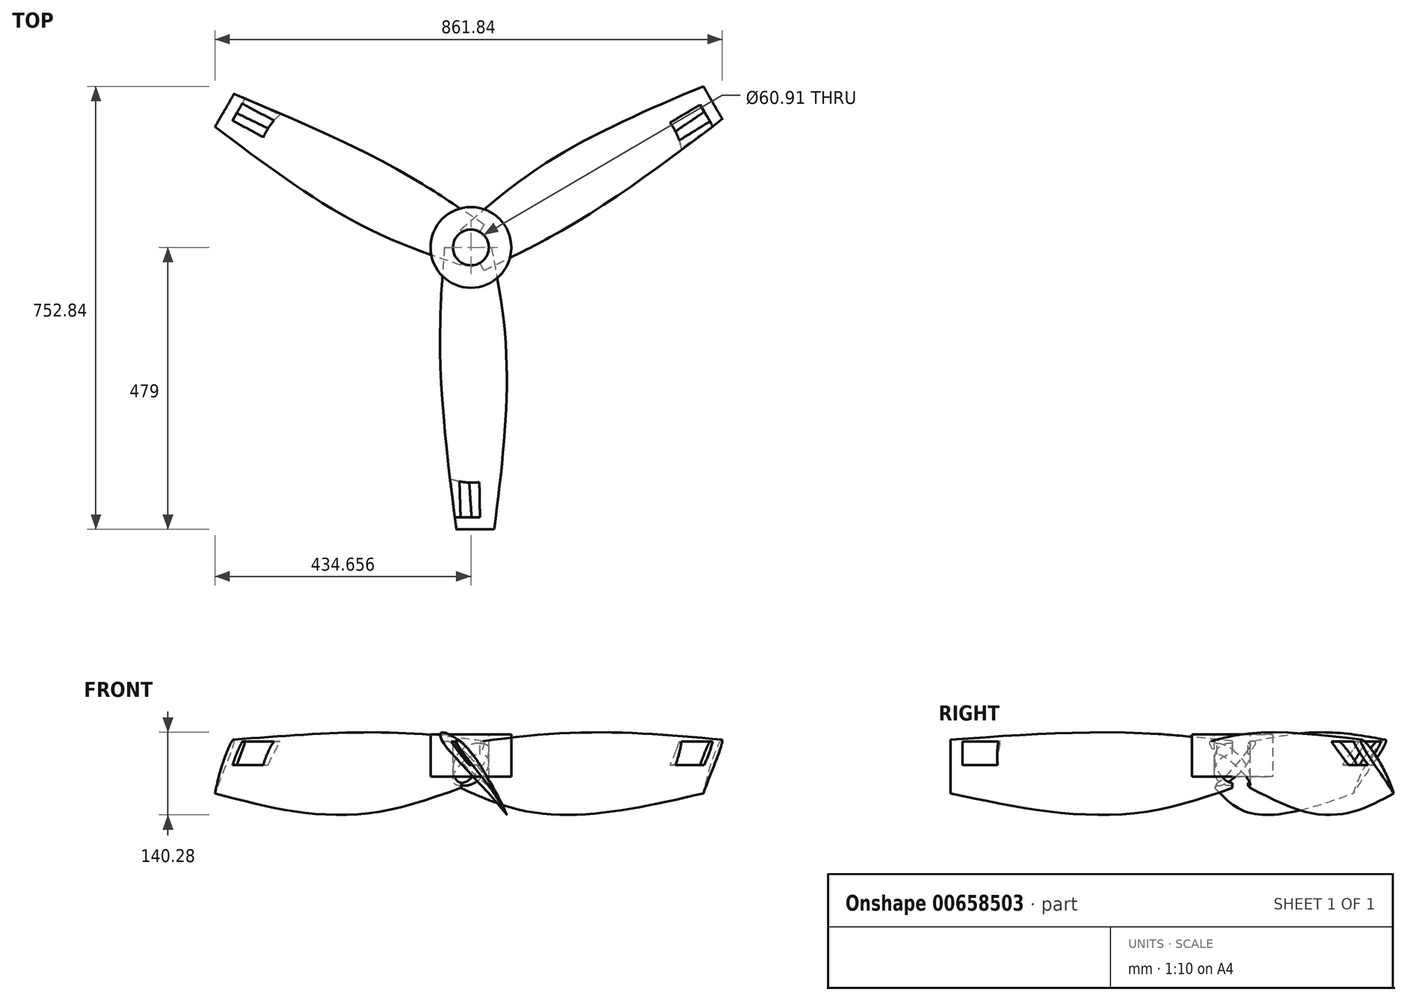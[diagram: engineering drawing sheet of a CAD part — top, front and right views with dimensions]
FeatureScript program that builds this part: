
annotation { "Feature Type Name" : "Feature", "Feature Type Description" : "" }
export const myFeature = defineFeature(function(context is Context, id is Id, definition is map)
    precondition{}
    {
        {
            var Q0;
            Q0=qCreatedBy(makeId("Front.planeOp"),FACE);
            var sketch = newSketch(context, id + "F0", { "sketchPlane" : qUnion([Q0])});
            skLineSegment(sketch, "E0", {"start": v(-19.7, 19.7) * mm, "end": v(0, 0) * mm, "construction": true});
            skLineSegment(sketch, "E1", {"start": v(0, 0) * mm, "end": v(19.7, -19.7) * mm, "construction": true});
            skLineSegment(sketch, "E2", {"start": v(19.7, -19.7) * mm, "end": v(39.39, -39.39) * mm, "construction": true});
            skLineSegment(sketch, "E3", {"start": v(39.39, -39.39) * mm, "end": v(59.08, -59.08) * mm, "construction": true});
            skLineSegment(sketch, "E4", {"start": v(0, 0) * mm, "end": v(7.36, 7.36) * mm, "construction": true});
            skLineSegment(sketch, "E5", {"start": v(-19.7, 19.7) * mm, "end": v(-16.01, 23.38) * mm, "construction": true});
            skFitSpline(sketch, "E6", {"points": [v(-19.7, 19.7) * mm, v(7.36, 7.36) * mm, v(59.08, -59.08) * mm], "startDerivative": vector(29.64, 29.64) * mm, "endDerivative": vector(58.96, -129.41) * mm});
            skPoint(sketch, "E7", {"position": v(3.68, 3.68) * mm});
            skLineSegment(sketch, "E8", {"start": v(-16.01, 23.38) * mm, "end": v(3.68, 3.68) * mm, "construction": true});
            skLineSegment(sketch, "E9", {"start": v(0, 0) * mm, "end": v(-3.68, -3.68) * mm, "construction": true});
            skLineSegment(sketch, "E10", {"start": v(-19.7, 19.7) * mm, "end": v(-23.38, 16.01) * mm, "construction": true});
            skFitSpline(sketch, "E11", {"points": [v(-19.7, 19.7) * mm, v(-3.68, -3.68) * mm, v(59.08, -59.08) * mm], "startDerivative": vector(-30.04, -30.04) * mm, "endDerivative": vector(93.45, -93.45) * mm});
            skLineSegment(sketch, "E12", {"start": v(39.39, -39.39) * mm, "end": v(46.75, -32.02) * mm, "construction": true});
            skLineSegment(sketch, "E13", {"start": v(0, 0) * mm, "end": v(-98.72, 0) * mm, "construction": true});
            skSolve(sketch);
        }
        {
            var Q0;
            Q0=qCreatedBy(makeId("Front.planeOp"),FACE);
            cPlane(context, id + "F1", {"entities" : qUnion([Q0]), "cplaneType" : CPlaneType.OFFSET, "offset" : 125 * mm, "width" : 150 * mm, "height" : 150 * mm});
        }
        {
            var Q0;
            Q0=qCreatedBy(id+"F1.planeOp",FACE);
            var sketch = newSketch(context, id + "F2", { "sketchPlane" : qUnion([Q0])});
            skLineSegment(sketch, "E14", {"start": v(-26.75, 31.88) * mm, "end": v(0, 0) * mm, "construction": true});
            skLineSegment(sketch, "E15", {"start": v(0, 0) * mm, "end": v(26.75, -31.88) * mm, "construction": true});
            skLineSegment(sketch, "E16", {"start": v(26.75, -31.88) * mm, "end": v(53.5, -63.76) * mm, "construction": true});
            skLineSegment(sketch, "E17", {"start": v(53.5, -63.76) * mm, "end": v(80.26, -95.64) * mm, "construction": true});
            skLineSegment(sketch, "E18", {"start": v(0, 0) * mm, "end": v(9.4, 7.88) * mm, "construction": true});
            skLineSegment(sketch, "E19", {"start": v(-26.75, 31.88) * mm, "end": v(-22.06, 35.82) * mm, "construction": true});
            skFitSpline(sketch, "E20", {"points": [v(-26.75, 31.88) * mm, v(9.4, 7.88) * mm, v(80.26, -95.64) * mm], "startDerivative": vector(38.04, 31.92) * mm, "endDerivative": vector(82.71, -189.43) * mm});
            skPoint(sketch, "E21", {"position": v(4.7, 3.94) * mm});
            skLineSegment(sketch, "E22", {"start": v(-22.06, 35.82) * mm, "end": v(4.7, 3.94) * mm, "construction": true});
            skLineSegment(sketch, "E23", {"start": v(0, 0) * mm, "end": v(-4.7, -3.94) * mm, "construction": true});
            skLineSegment(sketch, "E24", {"start": v(-26.75, 31.88) * mm, "end": v(-31.45, 27.94) * mm, "construction": true});
            skFitSpline(sketch, "E25", {"points": [v(-26.75, 31.88) * mm, v(-4.7, -3.94) * mm, v(80.26, -95.64) * mm], "startDerivative": vector(-38.37, -32.2) * mm, "endDerivative": vector(126.81, -151.13) * mm});
            skLineSegment(sketch, "E26", {"start": v(53.5, -63.76) * mm, "end": v(62.9, -55.88) * mm, "construction": true});
            skLineSegment(sketch, "E27", {"start": v(0, 0) * mm, "end": v(-123.06, 0) * mm, "construction": true});
            skSolve(sketch);
        }
        {
            var Q0;
            Q0=qCreatedBy(makeId("Front.planeOp"),FACE);
            cPlane(context, id + "F3", {"entities" : qUnion([Q0]), "cplaneType" : CPlaneType.OFFSET, "offset" : 479 * mm, "width" : 150 * mm, "height" : 150 * mm});
        }
        {
            var Q0;
            Q0=qCreatedBy(id+"F3.planeOp",FACE);
            var sketch = newSketch(context, id + "F4", { "sketchPlane" : qUnion([Q0])});
            skLineSegment(sketch, "E28", {"start": v(0.35, 22.72) * mm, "end": v(16.27, 0) * mm, "construction": true});
            skLineSegment(sketch, "E29", {"start": v(16.27, 0) * mm, "end": v(32.18, -22.72) * mm, "construction": true});
            skLineSegment(sketch, "E30", {"start": v(32.18, -22.72) * mm, "end": v(48.09, -45.45) * mm, "construction": true});
            skLineSegment(sketch, "E31", {"start": v(48.09, -45.45) * mm, "end": v(64, -68.17) * mm, "construction": true});
            skLineSegment(sketch, "E32", {"start": v(16.27, 0) * mm, "end": v(22.38, 4.28) * mm, "construction": true});
            skLineSegment(sketch, "E33", {"start": v(0.35, 22.72) * mm, "end": v(3.41, 24.87) * mm, "construction": true});
            skFitSpline(sketch, "E34", {"points": [v(0.35, 22.72) * mm, v(22.38, 4.28) * mm, v(64, -68.17) * mm], "startDerivative": vector(24.82, 17.38) * mm, "endDerivative": vector(46.62, -128.53) * mm});
            skPoint(sketch, "E35", {"position": v(19.32, 2.14) * mm});
            skLineSegment(sketch, "E36", {"start": v(3.41, 24.87) * mm, "end": v(19.32, 2.14) * mm, "construction": true});
            skLineSegment(sketch, "E37", {"start": v(16.27, 0) * mm, "end": v(13.2, -2.14) * mm, "construction": true});
            skLineSegment(sketch, "E38", {"start": v(0.35, 22.72) * mm, "end": v(-2.7, 20.58) * mm, "construction": true});
            skFitSpline(sketch, "E39", {"points": [v(0.35, 22.72) * mm, v(13.2, -2.14) * mm, v(64, -68.17) * mm], "startDerivative": vector(-25, -17.5) * mm, "endDerivative": vector(75.4, -107.69) * mm});
            skLineSegment(sketch, "E40", {"start": v(48.09, -45.45) * mm, "end": v(54.2, -41.17) * mm, "construction": true});
            skLineSegment(sketch, "E41", {"start": v(19.32, 2.14) * mm, "end": v(-38.53, 2.14) * mm, "construction": true});
            skSolve(sketch);
        }
        {
            var Q0;
            Q0=qSketchRegion(id+"F0",true);
            var Q1;
            Q1=qSketchRegion(id+"F2",true);
            var Q2;
            Q2=qSketchRegion(id+"F4",true);
            var Q3;
            Q3=sQuery(id+"F0.wireOp",VERTEX,"E6.1.internal");
            var Q4;
            Q4=sQuery(id+"F2.wireOp",VERTEX,"E20.1.internal");
            var Q5;
            Q5=sQuery(id+"F4.wireOp",VERTEX,"E32.end");
            loft(context, id + "F5", {"sheetProfilesArray" : [{ "sheetProfileEntities" : qUnion([Q0]) }, { "sheetProfileEntities" : qUnion([Q1]) }, { "sheetProfileEntities" : qUnion([Q2]) }], "matchConnections" : true, "connections" : [{ "connectionEntities" : qUnion([Q3, Q4, Q5]), "connectionEdgeQueries" : qUnion([]), "connectionEdgeParameters" : [] }]});
        }
        {
            var Q0;
            Q0=qCreatedBy(makeId("Top.planeOp"),FACE);
            var sketch = newSketch(context, id + "F6", { "sketchPlane" : qUnion([Q0])});
            skFitSpline(sketch, "E42", {"points": [v(-55.98, -360.47) * mm, v(39.38, -398.87) * mm, v(142.8, -333.19) * mm], "startDerivative": vector(111.22, -150.8) * mm, "endDerivative": vector(54.24, 145.78) * mm});
            skLineSegment(sketch, "E43", {"start": v(-55.98, -360.47) * mm, "end": v(-55.98, -458.75) * mm});
            skLineSegment(sketch, "E44", {"start": v(142.8, -333.19) * mm, "end": v(142.8, -458.75) * mm});
            skLineSegment(sketch, "E45", {"start": v(142.8, -458.75) * mm, "end": v(-55.98, -458.75) * mm});
            skSolve(sketch);
        }
        {
            var Q0;
            Q0=qSketchRegion(id+"F6",true);
            extrude(context, id + "F7", {"entities" : qUnion([Q0]), "operationType" : NewBodyOperationType.REMOVE, "endBound" : BoundingType.SYMMETRIC, "oppositeDirection" : true, "depth" : 40.17 * mm});
        }
        {
            var Q0;
            Q0=qCreatedBy(makeId("Top.planeOp"),FACE);
            var sketch = newSketch(context, id + "F8", { "sketchPlane" : qUnion([Q0])});
            skCircle(sketch, "E46", {"center": v(24.35, 0) * mm, "radius": 68.6 * mm});
            skSolve(sketch);
        }
        {
            var Q0;
            Q0=qSketchRegion(id+"F8",true);
            extrude(context, id + "F9", {"entities" : qUnion([Q0]), "depth" : 32.31 * mm, "hasSecondDirection" : true, "secondDirectionOppositeDirection" : true, "secondDirectionDepth" : 40 * mm});
        }
        {
            var Q0;
            Q0=makeQuery(id+"F5.opLoft","SWEPT_BODY",BODY,{"disambiguationData":[OSD([makeQuery(id+"F0.imprint","IMPRINT",FACE,{"disambiguationData":[TD([[makeQuery(id+"F0.imprint","IMPRINT",EDGE,{"derivedFrom":sQuery(id+"F0.wireOp",EDGE,"E6")}),-1.0]])]}),sQuery(id+"F2.wireOp",EDGE,"E25"),makeQuery(id+"F4.imprint","IMPRINT",FACE,{"disambiguationData":[TD([[makeQuery(id+"F4.imprint","IMPRINT",EDGE,{"derivedFrom":sQuery(id+"F4.wireOp",EDGE,"E34")}),-1.0]])]})])]});
            var Q1;
            Q1=makeQuery(id+"F9.opExtrude","SWEPT_FACE",FACE,{"disambiguationData":[OSD([sQuery(id+"F8.wireOp",EDGE,"E46")])]});
            circularPattern(context, id + "F10", {"entities" : qUnion([Q0]), "axis" : qUnion([Q1]), "angle" : 360 * degree, "instanceCount" : 3, "equalSpace" : true});
        }
        {
            var Q0;
            Q0=makeQuery(id+"F9.opExtrude","CAP_FACE",FACE,{"disambiguationData":[OSD([sQuery(id+"F8.wireOp",EDGE,"E46")])],"isStart":false});
            var sketch = newSketch(context, id + "F11", { "sketchPlane" : qUnion([Q0])});
            skCircle(sketch, "E47", {"center": v(24.35, 0) * mm, "radius": 30.45 * mm});
            skSolve(sketch);
        }
        {
            var Q0;
            Q0=qSketchRegion(id+"F11",true);
            extrude(context, id + "F12", {"entities" : qUnion([Q0]), "operationType" : NewBodyOperationType.REMOVE, "endBound" : BoundingType.THROUGH_ALL, "oppositeDirection" : true, "depth" : 25 * mm});
        }
    });
